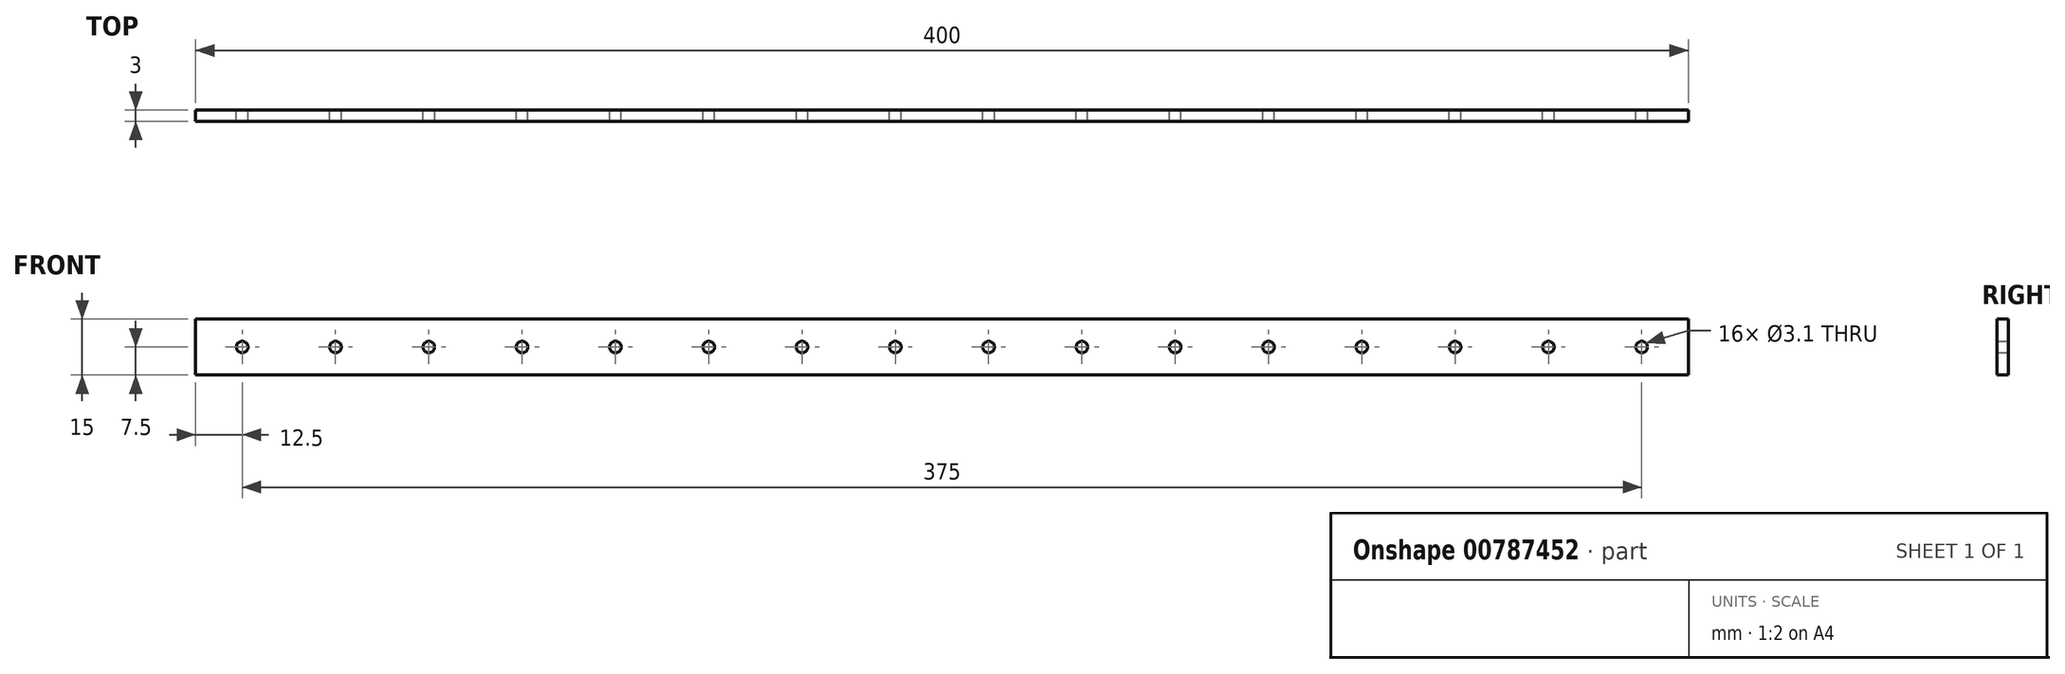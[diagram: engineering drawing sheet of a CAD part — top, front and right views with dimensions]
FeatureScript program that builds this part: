
annotation { "Feature Type Name" : "Feature", "Feature Type Description" : "" }
export const myFeature = defineFeature(function(context is Context, id is Id, definition is map)
    precondition{}
    {
        {
            var Q0;
            Q0=qCreatedBy(makeId("Front.planeOp"),FACE);
            var sketch = newSketch(context, id + "F0", { "sketchPlane" : qUnion([Q0])});
            skLineSegment(sketch, "E0.bottom", {"start": v(200, 7.5) * mm, "end": v(-200, 7.5) * mm});
            skLineSegment(sketch, "E0.top", {"start": v(200, -7.5) * mm, "end": v(-200, -7.5) * mm});
            skLineSegment(sketch, "E0.left", {"start": v(200, 7.5) * mm, "end": v(200, -7.5) * mm});
            skLineSegment(sketch, "E0.right", {"start": v(-200, 7.5) * mm, "end": v(-200, -7.5) * mm});
            skPoint(sketch, "E0.middle", {"position": v(0, 0) * mm});
            skLineSegment(sketch, "E1", {"start": v(-200, 0) * mm, "end": v(200, 0) * mm, "construction": true});
            skCircle(sketch, "E2", {"center": v(-187.5, 0) * mm, "radius": 1.55 * mm});
            skCircle(sketch, "E3.1.0.0", {"center": v(-162.5, 0) * mm, "radius": 1.55 * mm});
            skCircle(sketch, "E3.2.0.0", {"center": v(-137.5, 0) * mm, "radius": 1.55 * mm});
            skCircle(sketch, "E3.3.0.0", {"center": v(-112.5, 0) * mm, "radius": 1.55 * mm});
            skCircle(sketch, "E3.4.0.0", {"center": v(-87.5, 0) * mm, "radius": 1.55 * mm});
            skCircle(sketch, "E3.5.0.0", {"center": v(-62.5, 0) * mm, "radius": 1.55 * mm});
            skCircle(sketch, "E3.6.0.0", {"center": v(-37.5, 0) * mm, "radius": 1.55 * mm});
            skCircle(sketch, "E3.7.0.0", {"center": v(-12.5, 0) * mm, "radius": 1.55 * mm});
            skCircle(sketch, "E3.8.0.0", {"center": v(12.5, 0) * mm, "radius": 1.55 * mm});
            skCircle(sketch, "E3.9.0.0", {"center": v(37.5, 0) * mm, "radius": 1.55 * mm});
            skCircle(sketch, "E3.10.0.0", {"center": v(62.5, 0) * mm, "radius": 1.55 * mm});
            skCircle(sketch, "E3.11.0.0", {"center": v(87.5, 0) * mm, "radius": 1.55 * mm});
            skCircle(sketch, "E3.12.0.0", {"center": v(112.5, 0) * mm, "radius": 1.55 * mm});
            skCircle(sketch, "E3.13.0.0", {"center": v(137.5, 0) * mm, "radius": 1.55 * mm});
            skCircle(sketch, "E3.14.0.0", {"center": v(162.5, 0) * mm, "radius": 1.55 * mm});
            skCircle(sketch, "E3.15.0.0", {"center": v(187.5, 0) * mm, "radius": 1.55 * mm});
            skLineSegment(sketch, "E3.direction1", {"start": v(-187.5, 0) * mm, "end": v(-162.5, 0) * mm, "construction": true});
            skSolve(sketch);
        }
        {
            var Q0;
            Q0 = qSketchRegion(id + "F0", true);
            extrude(context, id + "F1", {"entities" : qUnion([Q0]), "depth" : 3 * mm, "offsetDistance" : 25 * mm});
        }
    });
